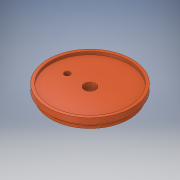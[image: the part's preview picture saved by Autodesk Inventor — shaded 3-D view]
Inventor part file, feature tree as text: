
AUTODESK INVENTOR PART (.ipt)
format: ipt  version: 2017 SP1 (Build 210196100, 196)  size: 144,896 bytes
history: native  units: in
note: dims shown in document units (in); Inventor stores cm internally (conversion verified against a paired STEP export)
features: extrude x5, sketch x5
ambient origin geometry x8: Origin, YZ Plane, XZ Plane, XY Plane, X Axis, Y Axis, Z Axis, Center Point
bodies: Solid1 (feature_tree)
feature tree (10):
  extrude  "Extrusion1"  Depth=0.25in TaperAngle=0.0deg
  extrude  "Extrusion2"  Depth=0.25in TaperAngle=0.0deg
  extrude  "Extrusion3"  Depth=0.25in TaperAngle=0.0deg
  extrude  "Extrusion4"  Depth=1.0in
  extrude  "Extrusion5"  Depth=0.25in TaperAngle=0.0deg
  sketch  "Sketch1"  dims[d0=6.9in d1=0.25in d2=0.0in]
  sketch  "Sketch2"  dims[d3=6.4in d4=0.25in d5=0.0in]
  sketch  "Sketch3"  dims[d6=7.4in d7=0.25in d8=0.0in]
  sketch  "Sketch4"  dims[d9=1.0in d10=2.0in]
  sketch  "Sketch5"  dims[d11=0.5in d12=0.25in d13=0.0in d14=7.4in d15=6.9in d16=0.25in d17=0.0in]
